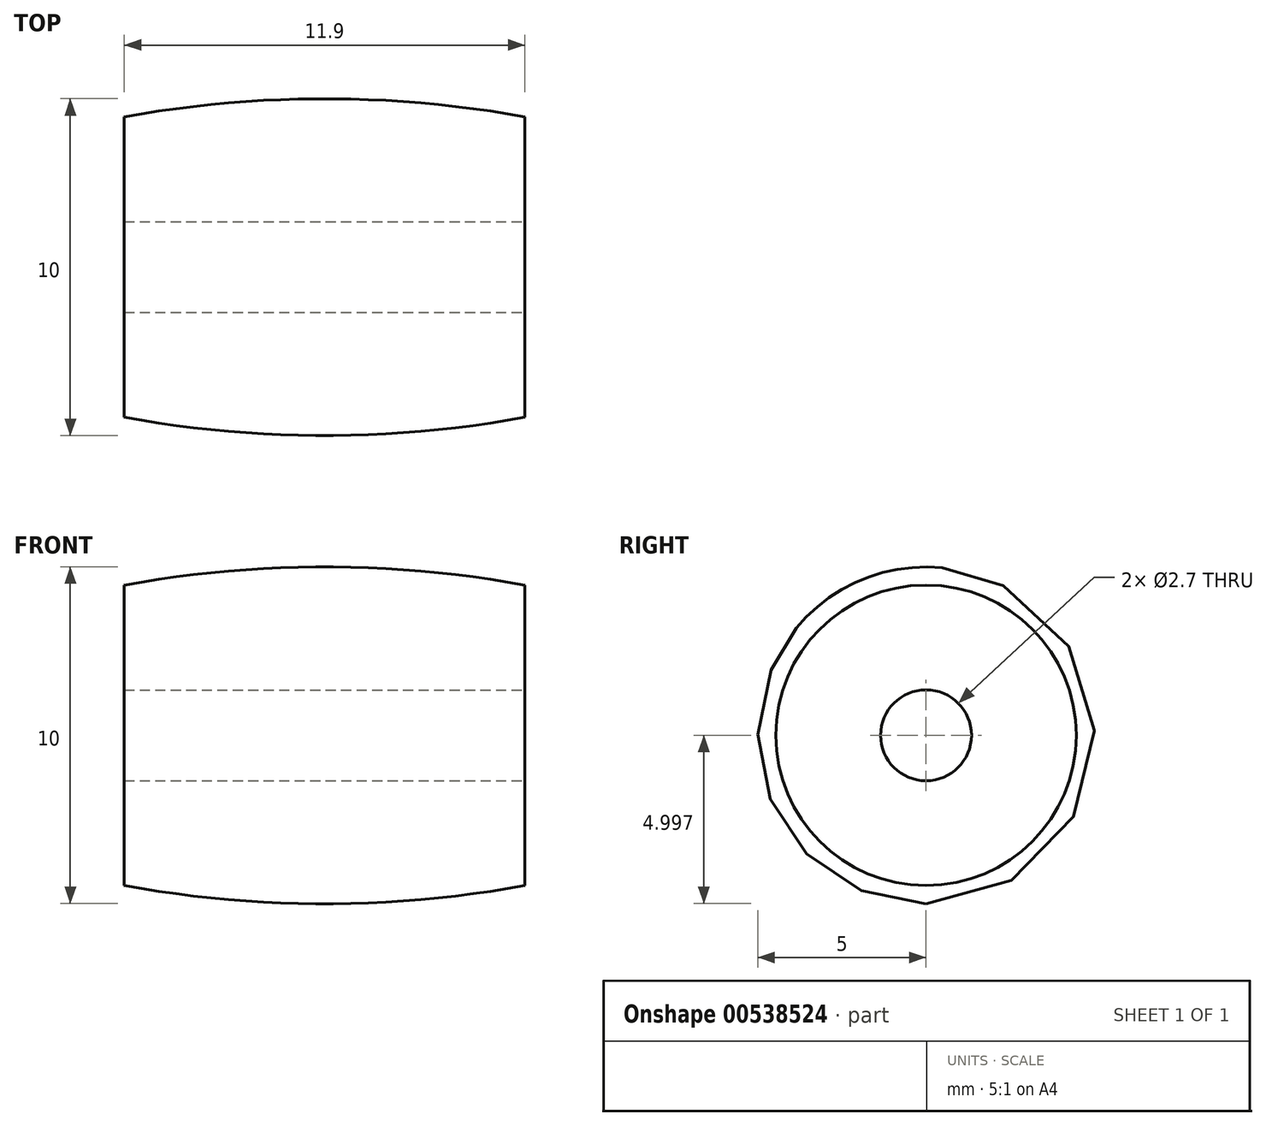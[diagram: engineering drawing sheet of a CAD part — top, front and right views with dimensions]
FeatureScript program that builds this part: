
annotation { "Feature Type Name" : "Feature", "Feature Type Description" : "" }
export const myFeature = defineFeature(function(context is Context, id is Id, definition is map)
    precondition{}
    {
        {
            var Q0;
            Q0=qCreatedBy(makeId("Front.planeOp"),FACE);
            var sketch = newSketch(context, id + "F0", { "sketchPlane" : qUnion([Q0])});
            skCircle(sketch, "E0", {"center": v(0, 0) * mm, "radius": 33.1 * mm});
            skLineSegment(sketch, "E1.bottom", {"start": v(5.95, 28.1) * mm, "end": v(-5.95, 28.1) * mm});
            skLineSegment(sketch, "E1.top", {"start": v(5.95, 38.1) * mm, "end": v(-5.95, 38.1) * mm});
            skLineSegment(sketch, "E1.left", {"start": v(5.95, 28.1) * mm, "end": v(5.95, 38.1) * mm});
            skLineSegment(sketch, "E1.right", {"start": v(-5.95, 28.1) * mm, "end": v(-5.95, 38.1) * mm});
            skPoint(sketch, "E1.middle", {"position": v(0, 33.1) * mm});
            skLineSegment(sketch, "E2", {"start": v(0, 33.1) * mm, "end": v(0, 0) * mm});
            skLineSegment(sketch, "E3", {"start": v(-5.95, 29.46) * mm, "end": v(5.95, 29.46) * mm});
            skSolve(sketch);
        }
        {
            var Q0;
            {var subQ0=sQuery(id+"F0.wireOp",EDGE,"E2");var subQ1=sQuery(id+"F0.wireOp",EDGE,"E0");var subQ2=makeQuery(id+"F0.imprint","INTERSECT",VERTEX,{"derivedFrom":[subQ1,subQ0]});Q0=makeQuery(id+"F0.imprint","IMPRINT",FACE,{"disambiguationData":[TD([[makeQuery(id+"F0.imprint","IMPRINT",EDGE,{"disambiguationData":[TD([[subQ2,-1.0]])],"derivedFrom":subQ1}),1.0]])]});}
            var Q1;
            {var subQ0=sQuery(id+"F0.wireOp",EDGE,"E2");var subQ1=sQuery(id+"F0.wireOp",EDGE,"E0");var subQ2=makeQuery(id+"F0.imprint","INTERSECT",VERTEX,{"derivedFrom":[subQ1,subQ0]});Q1=makeQuery(id+"F0.imprint","IMPRINT",FACE,{"disambiguationData":[TD([[makeQuery(id+"F0.imprint","IMPRINT",EDGE,{"disambiguationData":[TD([[subQ2,1.0]])],"derivedFrom":subQ1}),1.0]])]});}
            var Q2;
            Q2=sQuery(id+"F0.wireOp",EDGE,"E1.bottom");
            revolve(context, id + "F1", {"entities" : qUnion([Q0, Q1]), "axis" : qUnion([Q2]), "revolveType" : RevolveType.FULL});
        }
    });
